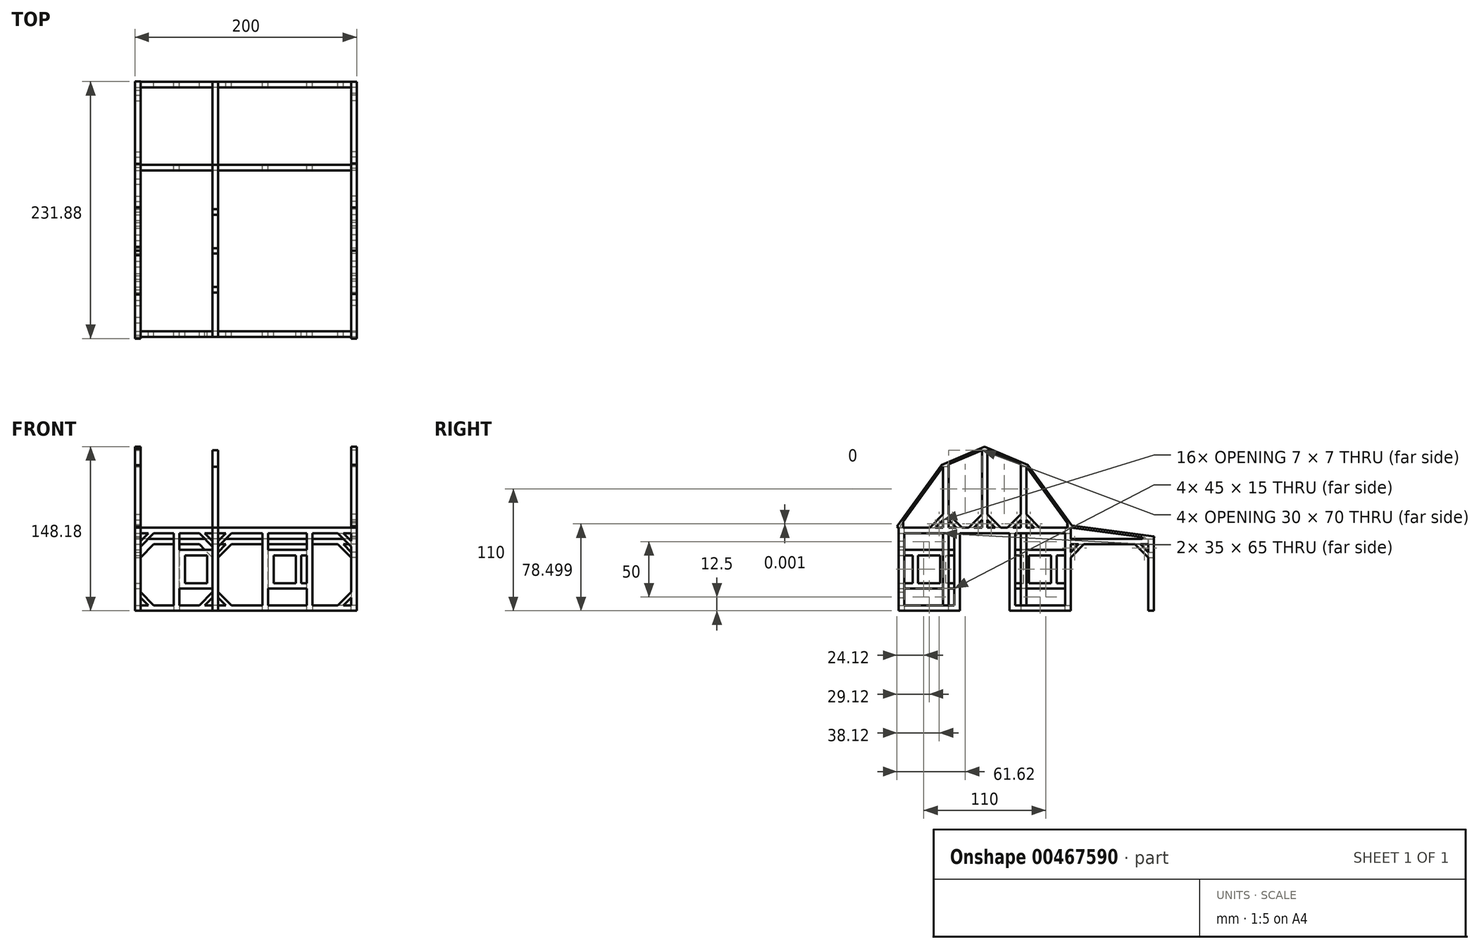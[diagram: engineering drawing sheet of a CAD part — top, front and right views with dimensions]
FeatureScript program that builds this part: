
annotation { "Feature Type Name" : "Feature", "Feature Type Description" : "" }
export const myFeature = defineFeature(function(context is Context, id is Id, definition is map)
    precondition{}
    {
        {
            var Q0;
            Q0=qCreatedBy(makeId("Front.planeOp"),FACE);
            var sketch = newSketch(context, id + "F0", { "sketchPlane" : qUnion([Q0])});
            skLineSegment(sketch, "E0", {"start": v(-73.98, 70) * mm, "end": v(-73.98, 65) * mm});
            skLineSegment(sketch, "E1", {"start": v(-73.98, 0) * mm, "end": v(-73.98, -5) * mm});
            skLineSegment(sketch, "E2", {"start": v(116.02, -5) * mm, "end": v(116.02, 0) * mm});
            skLineSegment(sketch, "E3", {"start": v(116.02, 70) * mm, "end": v(116.02, 65) * mm});
            skLineSegment(sketch, "E4", {"start": v(76.02, 65) * mm, "end": v(41.02, 65) * mm});
            skLineSegment(sketch, "E5", {"start": v(76.02, 0) * mm, "end": v(41.02, 0) * mm});
            skLineSegment(sketch, "E6", {"start": v(-8.98, 65) * mm, "end": v(-8.98, 70) * mm});
            skLineSegment(sketch, "E7", {"start": v(-3.98, 65) * mm, "end": v(-3.98, 70) * mm});
            skLineSegment(sketch, "E8", {"start": v(-8.98, 0) * mm, "end": v(-8.98, -5) * mm});
            skLineSegment(sketch, "E9", {"start": v(-3.98, 0) * mm, "end": v(-3.98, -5) * mm});
            skLineSegment(sketch, "E10", {"start": v(-73.98, 70) * mm, "end": v(-8.98, 70) * mm});
            skLineSegment(sketch, "E11", {"start": v(-73.98, -5) * mm, "end": v(-8.98, -5) * mm});
            skLineSegment(sketch, "E12", {"start": v(-3.98, 70) * mm, "end": v(116.02, 70) * mm});
            skLineSegment(sketch, "E13", {"start": v(-3.98, -5) * mm, "end": v(116.02, -5) * mm});
            skLineSegment(sketch, "E14", {"start": v(-73.98, 58) * mm, "end": v(-73.98, 53) * mm});
            skLineSegment(sketch, "E15", {"start": v(-73.98, 65) * mm, "end": v(-66.98, 65) * mm});
            skLineSegment(sketch, "E16", {"start": v(-73.98, 58) * mm, "end": v(-66.98, 65) * mm});
            skLineSegment(sketch, "E17", {"start": v(-73.98, 53) * mm, "end": v(-61.98, 65) * mm});
            skLineSegment(sketch, "E18", {"start": v(-73.98, 7) * mm, "end": v(-73.98, 12) * mm});
            skLineSegment(sketch, "E19", {"start": v(-73.98, 0) * mm, "end": v(-66.98, 0) * mm});
            skLineSegment(sketch, "E20", {"start": v(-66.98, 0) * mm, "end": v(-73.98, 7) * mm});
            skLineSegment(sketch, "E21", {"start": v(-61.98, 0) * mm, "end": v(-73.98, 12) * mm});
            skLineSegment(sketch, "E22", {"start": v(-8.98, 65) * mm, "end": v(-15.98, 65) * mm});
            skLineSegment(sketch, "E23", {"start": v(-8.98, 58) * mm, "end": v(-8.98, 53) * mm});
            skLineSegment(sketch, "E24", {"start": v(-15.98, 65) * mm, "end": v(-8.98, 58) * mm});
            skLineSegment(sketch, "E25", {"start": v(-20.98, 65) * mm, "end": v(-8.98, 53) * mm});
            skLineSegment(sketch, "E26", {"start": v(-8.98, 7) * mm, "end": v(-8.98, 12) * mm});
            skLineSegment(sketch, "E27", {"start": v(-8.98, 0) * mm, "end": v(-15.98, 0) * mm});
            skLineSegment(sketch, "E28", {"start": v(-15.98, 0) * mm, "end": v(-8.98, 7) * mm});
            skLineSegment(sketch, "E29", {"start": v(-20.98, 0) * mm, "end": v(-8.98, 12) * mm});
            skLineSegment(sketch, "E30", {"start": v(-3.98, 58) * mm, "end": v(-3.98, 53) * mm});
            skLineSegment(sketch, "E31", {"start": v(-3.98, 7) * mm, "end": v(-3.98, 12) * mm});
            skLineSegment(sketch, "E32", {"start": v(-3.98, 65) * mm, "end": v(3.02, 65) * mm});
            skLineSegment(sketch, "E33", {"start": v(-3.98, 58) * mm, "end": v(3.02, 65) * mm});
            skLineSegment(sketch, "E34", {"start": v(-3.98, 53) * mm, "end": v(8.02, 65) * mm});
            skLineSegment(sketch, "E35", {"start": v(-3.98, 0) * mm, "end": v(3.02, 0) * mm});
            skLineSegment(sketch, "E36", {"start": v(-3.98, 7) * mm, "end": v(3.02, 0) * mm});
            skLineSegment(sketch, "E37", {"start": v(-3.98, 12) * mm, "end": v(8.02, 0) * mm});
            skLineSegment(sketch, "E38", {"start": v(116.02, 65) * mm, "end": v(109.02, 65) * mm});
            skLineSegment(sketch, "E39", {"start": v(116.02, 58) * mm, "end": v(116.02, 53) * mm});
            skLineSegment(sketch, "E40", {"start": v(109.02, 65) * mm, "end": v(116.02, 58) * mm});
            skLineSegment(sketch, "E41", {"start": v(104.02, 65) * mm, "end": v(116.02, 53) * mm});
            skLineSegment(sketch, "E42", {"start": v(116.02, 7) * mm, "end": v(116.02, 12) * mm});
            skLineSegment(sketch, "E43", {"start": v(116.02, 0) * mm, "end": v(109.02, 0) * mm});
            skLineSegment(sketch, "E44", {"start": v(109.02, 0) * mm, "end": v(116.02, 7) * mm});
            skLineSegment(sketch, "E45", {"start": v(104.02, 0) * mm, "end": v(116.02, 12) * mm});
            skLineSegment(sketch, "E46", {"start": v(-61.98, 65) * mm, "end": v(-43.98, 65) * mm});
            skLineSegment(sketch, "E47", {"start": v(-61.98, 0) * mm, "end": v(-43.98, 0) * mm});
            skLineSegment(sketch, "E48", {"start": v(-20.98, 65) * mm, "end": v(-38.98, 65) * mm});
            skLineSegment(sketch, "E49", {"start": v(8.02, 65) * mm, "end": v(36.02, 65) * mm});
            skLineSegment(sketch, "E50", {"start": v(-20.98, 0) * mm, "end": v(-38.98, 0) * mm});
            skLineSegment(sketch, "E51", {"start": v(104.02, 65) * mm, "end": v(81.02, 65) * mm});
            skLineSegment(sketch, "E52", {"start": v(104.02, 0) * mm, "end": v(81.02, 0) * mm});
            skLineSegment(sketch, "E53", {"start": v(8.02, 0) * mm, "end": v(36.02, 0) * mm});
            skLineSegment(sketch, "E54", {"start": v(-43.98, 65) * mm, "end": v(-43.98, 0) * mm});
            skLineSegment(sketch, "E55", {"start": v(36.02, 65) * mm, "end": v(36.02, 0) * mm});
            skLineSegment(sketch, "E56", {"start": v(81.02, 65) * mm, "end": v(81.02, 0) * mm});
            skLineSegment(sketch, "E57", {"start": v(41.02, 0) * mm, "end": v(41.02, 15) * mm});
            skLineSegment(sketch, "E58", {"start": v(41.02, 50) * mm, "end": v(41.02, 65) * mm});
            skLineSegment(sketch, "E59", {"start": v(76.02, 0) * mm, "end": v(76.02, 15) * mm});
            skLineSegment(sketch, "E60", {"start": v(76.02, 20) * mm, "end": v(76.02, 45) * mm});
            skLineSegment(sketch, "E61", {"start": v(76.02, 50) * mm, "end": v(76.02, 65) * mm});
            skLineSegment(sketch, "E62", {"start": v(41.02, 50) * mm, "end": v(76.02, 50) * mm});
            skLineSegment(sketch, "E63", {"start": v(41.02, 15) * mm, "end": v(76.02, 15) * mm});
            skLineSegment(sketch, "E64", {"start": v(76.02, 20) * mm, "end": v(71.02, 20) * mm});
            skLineSegment(sketch, "E65", {"start": v(76.02, 45) * mm, "end": v(71.02, 45) * mm});
            skLineSegment(sketch, "E66", {"start": v(71.02, 45) * mm, "end": v(71.02, 20) * mm});
            skLineSegment(sketch, "E67", {"start": v(46.02, 45) * mm, "end": v(46.02, 20) * mm});
            skLineSegment(sketch, "E68", {"start": v(46.02, 45) * mm, "end": v(66.02, 45) * mm});
            skLineSegment(sketch, "E69", {"start": v(46.02, 20) * mm, "end": v(66.02, 20) * mm});
            skLineSegment(sketch, "E70", {"start": v(66.02, 45) * mm, "end": v(66.02, 20) * mm});
            skLineSegment(sketch, "E71", {"start": v(-38.98, 0) * mm, "end": v(-38.98, 15) * mm});
            skLineSegment(sketch, "E72", {"start": v(-38.98, 50) * mm, "end": v(-38.98, 65) * mm});
            skLineSegment(sketch, "E73", {"start": v(-38.98, 15) * mm, "end": v(-8.98, 15) * mm});
            skLineSegment(sketch, "E74", {"start": v(-38.98, 50) * mm, "end": v(-8.98, 50) * mm});
            skLineSegment(sketch, "E75", {"start": v(-33.98, 45) * mm, "end": v(-33.98, 20) * mm});
            skLineSegment(sketch, "E76", {"start": v(-13.98, 45) * mm, "end": v(-13.98, 20) * mm});
            skLineSegment(sketch, "E77", {"start": v(-33.98, 20) * mm, "end": v(-13.98, 20) * mm});
            skLineSegment(sketch, "E78", {"start": v(-33.98, 45) * mm, "end": v(-13.98, 45) * mm});
            skLineSegment(sketch, "E79", {"start": v(-8.98, 15) * mm, "end": v(-8.98, 50) * mm});
            skSolve(sketch);
        }
        {
            var Q0;
            Q0 = qSketchRegion(id + "F0", true);
            extrude(context, id + "F1", {"entities" : qUnion([Q0]), "depth" : 5 * mm});
        }
        {
            var Q0;
            Q0=makeQuery(id+"F1.opExtrude","SWEPT_FACE",FACE,{"disambiguationData":[OSD([sQuery(id+"F0.wireOp",EDGE,"E1")])]});
            var sketch = newSketch(context, id + "F2", { "sketchPlane" : qUnion([Q0])});
            skLineSegment(sketch, "E80", {"start": v(5, -5) * mm, "end": v(5, 70) * mm});
            skLineSegment(sketch, "E81", {"start": v(-150, 70) * mm, "end": v(-150, 60) * mm});
            skLineSegment(sketch, "E82", {"start": v(-225, 60) * mm, "end": v(-225, -5) * mm});
            skLineSegment(sketch, "E83", {"start": v(-225, -5) * mm, "end": v(-220, -5) * mm});
            skLineSegment(sketch, "E84", {"start": v(-150, 55) * mm, "end": v(-150, 48) * mm});
            skLineSegment(sketch, "E85", {"start": v(-150, 55) * mm, "end": v(-157, 55) * mm});
            skLineSegment(sketch, "E86", {"start": v(-157, 55) * mm, "end": v(-150, 48) * mm});
            skLineSegment(sketch, "E87", {"start": v(-162, 55) * mm, "end": v(-150, 43) * mm});
            skLineSegment(sketch, "E88", {"start": v(-220, 55) * mm, "end": v(-220, 48) * mm});
            skLineSegment(sketch, "E89", {"start": v(-220, 55) * mm, "end": v(-213, 55) * mm});
            skLineSegment(sketch, "E90", {"start": v(-220, 48) * mm, "end": v(-213, 55) * mm});
            skLineSegment(sketch, "E91", {"start": v(-220, 43) * mm, "end": v(-208, 55) * mm});
            skLineSegment(sketch, "E92", {"start": v(-110, 70) * mm, "end": v(-110, 77) * mm});
            skLineSegment(sketch, "E93", {"start": v(-110, 70) * mm, "end": v(-117, 70) * mm});
            skLineSegment(sketch, "E94", {"start": v(-117, 70) * mm, "end": v(-110, 77) * mm});
            skLineSegment(sketch, "E95", {"start": v(-122, 70) * mm, "end": v(-110, 82) * mm});
            skLineSegment(sketch, "E96", {"start": v(-105, 70) * mm, "end": v(-105, 77) * mm});
            skLineSegment(sketch, "E97", {"start": v(-105, 70) * mm, "end": v(-98, 70) * mm});
            skLineSegment(sketch, "E98", {"start": v(-98, 70) * mm, "end": v(-105, 77) * mm});
            skLineSegment(sketch, "E99", {"start": v(-93, 70) * mm, "end": v(-105, 82) * mm});
            skLineSegment(sketch, "E100", {"start": v(-75, 70) * mm, "end": v(-75, 77) * mm});
            skLineSegment(sketch, "E101", {"start": v(-75, 70) * mm, "end": v(-82, 70) * mm});
            skLineSegment(sketch, "E102", {"start": v(-82, 70) * mm, "end": v(-75, 77) * mm});
            skLineSegment(sketch, "E103", {"start": v(-87, 70) * mm, "end": v(-75, 82) * mm});
            skLineSegment(sketch, "E104", {"start": v(-70, 70) * mm, "end": v(-70, 77) * mm});
            skLineSegment(sketch, "E105", {"start": v(-70, 70) * mm, "end": v(-63, 70) * mm});
            skLineSegment(sketch, "E106", {"start": v(-70, 77) * mm, "end": v(-63, 70) * mm});
            skLineSegment(sketch, "E107", {"start": v(-58, 70) * mm, "end": v(-70, 82) * mm});
            skLineSegment(sketch, "E108", {"start": v(-40, 70) * mm, "end": v(-40, 77) * mm});
            skLineSegment(sketch, "E109", {"start": v(-40, 70) * mm, "end": v(-47, 70) * mm});
            skLineSegment(sketch, "E110", {"start": v(-47, 70) * mm, "end": v(-40, 77) * mm});
            skLineSegment(sketch, "E111", {"start": v(-52, 70) * mm, "end": v(-40, 82) * mm});
            skLineSegment(sketch, "E112", {"start": v(-35, 70) * mm, "end": v(-35, 77) * mm});
            skLineSegment(sketch, "E113", {"start": v(-35, 70) * mm, "end": v(-28, 70) * mm});
            skLineSegment(sketch, "E114", {"start": v(-28, 70) * mm, "end": v(-35, 77) * mm});
            skLineSegment(sketch, "E115", {"start": v(-23, 70) * mm, "end": v(-35, 82) * mm});
            skLineSegment(sketch, "E116", {"start": v(5, 70) * mm, "end": v(6.62, 71.18) * mm});
            skLineSegment(sketch, "E117", {"start": v(6.62, 71.18) * mm, "end": v(-33.35, 126.13) * mm});
            skLineSegment(sketch, "E118", {"start": v(-33.35, 126.13) * mm, "end": v(-68.47, 141.18) * mm});
            skLineSegment(sketch, "E119", {"start": v(-68.47, 141.18) * mm, "end": v(-72.5, 143.18) * mm});
            skLineSegment(sketch, "E120", {"start": v(-225, 60) * mm, "end": v(-225.26, 61.98) * mm});
            skLineSegment(sketch, "E121", {"start": v(-225.26, 61.98) * mm, "end": v(-151.2, 71.85) * mm});
            skLineSegment(sketch, "E122", {"start": v(-151.2, 71.85) * mm, "end": v(-111.54, 126.4) * mm});
            skLineSegment(sketch, "E123", {"start": v(-111.54, 126.4) * mm, "end": v(-76.19, 141.55) * mm});
            skLineSegment(sketch, "E124", {"start": v(-76.19, 141.55) * mm, "end": v(-72.5, 143.18) * mm});
            skLineSegment(sketch, "E125", {"start": v(-70, 140) * mm, "end": v(-40, 127.14) * mm});
            skLineSegment(sketch, "E126", {"start": v(-75, 140) * mm, "end": v(-105, 127.14) * mm});
            skLineSegment(sketch, "E127", {"start": v(-147.9, 72.9) * mm, "end": v(-147.9, 70) * mm});
            skLineSegment(sketch, "E128", {"start": v(-110, 125) * mm, "end": v(-147.9, 72.9) * mm});
            skLineSegment(sketch, "E129", {"start": v(-147.9, 70) * mm, "end": v(-122, 70) * mm});
            skLineSegment(sketch, "E130", {"start": v(-110, 125) * mm, "end": v(-110, 82) * mm});
            skLineSegment(sketch, "E131", {"start": v(3.62, 71.9) * mm, "end": v(3.62, 70) * mm});
            skLineSegment(sketch, "E132", {"start": v(-35, 125) * mm, "end": v(3.62, 71.9) * mm});
            skLineSegment(sketch, "E133", {"start": v(-23, 70) * mm, "end": v(3.62, 70) * mm});
            skLineSegment(sketch, "E134", {"start": v(-35, 125) * mm, "end": v(-35, 82) * mm});
            skLineSegment(sketch, "E135", {"start": v(-217.53, 61) * mm, "end": v(-217.53, 60) * mm});
            skLineSegment(sketch, "E136", {"start": v(-217.53, 60) * mm, "end": v(-150, 60) * mm});
            skLineSegment(sketch, "E137", {"start": v(-217.53, 61) * mm, "end": v(-150, 70) * mm});
            skLineSegment(sketch, "E138", {"start": v(-220, 43) * mm, "end": v(-220, -5) * mm});
            skLineSegment(sketch, "E139", {"start": v(-208, 55) * mm, "end": v(-162, 55) * mm});
            skLineSegment(sketch, "E140", {"start": v(-150, 43) * mm, "end": v(-150, -5) * mm});
            skLineSegment(sketch, "E141", {"start": v(-93, 70) * mm, "end": v(-87, 70) * mm});
            skLineSegment(sketch, "E142", {"start": v(-58, 70) * mm, "end": v(-52, 70) * mm});
            skLineSegment(sketch, "E143", {"start": v(-75, 82) * mm, "end": v(-75, 140) * mm});
            skLineSegment(sketch, "E144", {"start": v(-70, 140) * mm, "end": v(-70, 82) * mm});
            skLineSegment(sketch, "E145", {"start": v(-40, 127.14) * mm, "end": v(-40, 82) * mm});
            skLineSegment(sketch, "E146", {"start": v(-105, 127.14) * mm, "end": v(-105, 82) * mm});
            skLineSegment(sketch, "E147", {"start": v(5, -5) * mm, "end": v(-50, -5) * mm});
            skPoint(sketch, "E147.endSnap0", {"position": v(2.5, -5) * mm});
            skLineSegment(sketch, "E148", {"start": v(-50, -5) * mm, "end": v(-50, 65) * mm});
            skLineSegment(sketch, "E149", {"start": v(-150, -5) * mm, "end": v(-95, -5) * mm});
            skLineSegment(sketch, "E150", {"start": v(-95, -5) * mm, "end": v(-95, 65) * mm});
            skLineSegment(sketch, "E151", {"start": v(-95, 65) * mm, "end": v(-50, 65) * mm});
            skLineSegment(sketch, "E152", {"start": v(-145, 65) * mm, "end": v(-100, 65) * mm});
            skLineSegment(sketch, "E153", {"start": v(-145, 0) * mm, "end": v(-100, 0) * mm});
            skLineSegment(sketch, "E154", {"start": v(-45, 65) * mm, "end": v(0, 65) * mm});
            skLineSegment(sketch, "E155", {"start": v(-45, 0) * mm, "end": v(0, 0) * mm});
            skLineSegment(sketch, "E156", {"start": v(-145, 15) * mm, "end": v(-100, 15) * mm});
            skLineSegment(sketch, "E157", {"start": v(-145, 20) * mm, "end": v(-137.5, 20) * mm});
            skLineSegment(sketch, "E158", {"start": v(-100, 20) * mm, "end": v(-107.5, 20) * mm});
            skLineSegment(sketch, "E159", {"start": v(-107.5, 20) * mm, "end": v(-107.5, 45) * mm});
            skLineSegment(sketch, "E160", {"start": v(-137.5, 20) * mm, "end": v(-137.5, 45) * mm});
            skLineSegment(sketch, "E161", {"start": v(-137.5, 45) * mm, "end": v(-145, 45) * mm});
            skLineSegment(sketch, "E162", {"start": v(-107.5, 45) * mm, "end": v(-100, 45) * mm});
            skLineSegment(sketch, "E163", {"start": v(-145, 50) * mm, "end": v(-100, 50) * mm});
            skLineSegment(sketch, "E164", {"start": v(-132.5, 20) * mm, "end": v(-112.5, 20) * mm});
            skLineSegment(sketch, "E165", {"start": v(-132.5, 45) * mm, "end": v(-132.5, 20) * mm});
            skLineSegment(sketch, "E166", {"start": v(-132.5, 45) * mm, "end": v(-112.5, 45) * mm});
            skLineSegment(sketch, "E167", {"start": v(-112.5, 45) * mm, "end": v(-112.5, 20) * mm});
            skLineSegment(sketch, "E168", {"start": v(-45, 15) * mm, "end": v(0, 15) * mm});
            skLineSegment(sketch, "E169", {"start": v(-45, 20) * mm, "end": v(-37.5, 20) * mm});
            skLineSegment(sketch, "E170", {"start": v(0, 20) * mm, "end": v(-7.5, 20) * mm});
            skLineSegment(sketch, "E171", {"start": v(-37.5, 20) * mm, "end": v(-37.5, 45) * mm});
            skLineSegment(sketch, "E172", {"start": v(-7.5, 20) * mm, "end": v(-7.5, 45) * mm});
            skLineSegment(sketch, "E173", {"start": v(-7.5, 45) * mm, "end": v(0, 45) * mm});
            skLineSegment(sketch, "E174", {"start": v(-37.5, 45) * mm, "end": v(-45, 45) * mm});
            skLineSegment(sketch, "E175", {"start": v(-45, 50) * mm, "end": v(0, 50) * mm});
            skLineSegment(sketch, "E176", {"start": v(-32.5, 45) * mm, "end": v(-32.5, 20) * mm});
            skLineSegment(sketch, "E177", {"start": v(-32.5, 45) * mm, "end": v(-12.5, 45) * mm});
            skLineSegment(sketch, "E178", {"start": v(-12.5, 45) * mm, "end": v(-12.5, 20) * mm});
            skLineSegment(sketch, "E179", {"start": v(-32.5, 20) * mm, "end": v(-12.5, 20) * mm});
            skLineSegment(sketch, "E180", {"start": v(-145, 65) * mm, "end": v(-145, 50) * mm});
            skLineSegment(sketch, "E181", {"start": v(-145, 45) * mm, "end": v(-145, 20) * mm});
            skLineSegment(sketch, "E182", {"start": v(-145, 15) * mm, "end": v(-145, 0) * mm});
            skLineSegment(sketch, "E183", {"start": v(-100, 65) * mm, "end": v(-100, 50) * mm});
            skLineSegment(sketch, "E184", {"start": v(-100, 45) * mm, "end": v(-100, 20) * mm});
            skLineSegment(sketch, "E185", {"start": v(-100, 15) * mm, "end": v(-100, 0) * mm});
            skLineSegment(sketch, "E186", {"start": v(-45, 65) * mm, "end": v(-45, 50) * mm});
            skLineSegment(sketch, "E187", {"start": v(-45, 45) * mm, "end": v(-45, 20) * mm});
            skLineSegment(sketch, "E188", {"start": v(-45, 15) * mm, "end": v(-45, 0) * mm});
            skLineSegment(sketch, "E189", {"start": v(0, 65) * mm, "end": v(0, 50) * mm});
            skLineSegment(sketch, "E190", {"start": v(0, 45) * mm, "end": v(0, 20) * mm});
            skLineSegment(sketch, "E191", {"start": v(0, 15) * mm, "end": v(0, 0) * mm});
            skSolve(sketch);
        }
        {
            var Q0;
            Q0 = qSketchRegion(id + "F2", true);
            extrude(context, id + "F3", {"entities" : qUnion([Q0]), "depth" : 5 * mm});
        }
        {
            var Q0;
            Q0=makeQuery(id+"F1.opExtrude","SWEPT_FACE",FACE,{"disambiguationData":[OSD([sQuery(id+"F0.wireOp",EDGE,"E3")])]});
            var sketch = newSketch(context, id + "F4", { "sketchPlane" : qUnion([Q0])});
            skLineSegment(sketch, "E192", {"start": v(-5, -5) * mm, "end": v(50, -5) * mm});
            skLineSegment(sketch, "E193", {"start": v(50, -5) * mm, "end": v(50, 65) * mm});
            skLineSegment(sketch, "E194", {"start": v(50, 65) * mm, "end": v(95, 65) * mm});
            skLineSegment(sketch, "E195", {"start": v(95, 65) * mm, "end": v(95, -5) * mm});
            skLineSegment(sketch, "E196", {"start": v(95, -5) * mm, "end": v(150, -5) * mm});
            skLineSegment(sketch, "E197", {"start": v(150, 60) * mm, "end": v(150, 70) * mm});
            skLineSegment(sketch, "E198", {"start": v(45, 65) * mm, "end": v(45, 0) * mm});
            skLineSegment(sketch, "E199", {"start": v(45, 0) * mm, "end": v(0, 0) * mm});
            skLineSegment(sketch, "E200", {"start": v(0, 0) * mm, "end": v(0, 65) * mm});
            skLineSegment(sketch, "E201", {"start": v(0, 65) * mm, "end": v(45, 65) * mm});
            skLineSegment(sketch, "E202", {"start": v(100, 65) * mm, "end": v(100, 0) * mm});
            skLineSegment(sketch, "E203", {"start": v(100, 0) * mm, "end": v(145, 0) * mm});
            skLineSegment(sketch, "E204", {"start": v(145, 0) * mm, "end": v(145, 65) * mm});
            skLineSegment(sketch, "E205", {"start": v(145, 65) * mm, "end": v(100, 65) * mm});
            skLineSegment(sketch, "E206", {"start": v(225, -5) * mm, "end": v(220, -5) * mm});
            skLineSegment(sketch, "E207", {"start": v(150, 55) * mm, "end": v(150, 48) * mm});
            skLineSegment(sketch, "E208", {"start": v(150, 55) * mm, "end": v(157, 55) * mm});
            skLineSegment(sketch, "E209", {"start": v(150, 48) * mm, "end": v(157, 55) * mm});
            skLineSegment(sketch, "E210", {"start": v(150, 43) * mm, "end": v(162, 55) * mm});
            skLineSegment(sketch, "E211", {"start": v(220, 55) * mm, "end": v(220, 48) * mm});
            skLineSegment(sketch, "E212", {"start": v(220, 55) * mm, "end": v(213, 55) * mm});
            skLineSegment(sketch, "E213", {"start": v(213, 55) * mm, "end": v(220, 48) * mm});
            skLineSegment(sketch, "E214", {"start": v(208, 55) * mm, "end": v(220, 43) * mm});
            skLineSegment(sketch, "E215", {"start": v(110, 70) * mm, "end": v(110, 77) * mm});
            skLineSegment(sketch, "E216", {"start": v(110, 70) * mm, "end": v(117, 70) * mm});
            skLineSegment(sketch, "E217", {"start": v(122, 70) * mm, "end": v(110, 82) * mm});
            skLineSegment(sketch, "E218", {"start": v(110, 77) * mm, "end": v(117, 70) * mm});
            skLineSegment(sketch, "E219", {"start": v(105, 70) * mm, "end": v(105, 77) * mm});
            skLineSegment(sketch, "E220", {"start": v(105, 70) * mm, "end": v(98, 70) * mm});
            skLineSegment(sketch, "E221", {"start": v(98, 70) * mm, "end": v(105, 77) * mm});
            skLineSegment(sketch, "E222", {"start": v(93, 70) * mm, "end": v(105, 82) * mm});
            skLineSegment(sketch, "E223", {"start": v(75, 70) * mm, "end": v(75, 77) * mm});
            skLineSegment(sketch, "E224", {"start": v(75, 70) * mm, "end": v(82, 70) * mm});
            skLineSegment(sketch, "E225", {"start": v(75, 77) * mm, "end": v(82, 70) * mm});
            skLineSegment(sketch, "E226", {"start": v(75, 82) * mm, "end": v(87, 70) * mm});
            skLineSegment(sketch, "E227", {"start": v(70, 70) * mm, "end": v(70, 77) * mm});
            skLineSegment(sketch, "E228", {"start": v(70, 70) * mm, "end": v(63, 70) * mm});
            skLineSegment(sketch, "E229", {"start": v(63, 70) * mm, "end": v(70, 77) * mm});
            skLineSegment(sketch, "E230", {"start": v(58, 70) * mm, "end": v(70, 82) * mm});
            skLineSegment(sketch, "E231", {"start": v(40, 70) * mm, "end": v(40, 77) * mm});
            skLineSegment(sketch, "E232", {"start": v(40, 70) * mm, "end": v(47, 70) * mm});
            skLineSegment(sketch, "E233", {"start": v(40, 77) * mm, "end": v(47, 70) * mm});
            skLineSegment(sketch, "E234", {"start": v(40, 82) * mm, "end": v(52, 70) * mm});
            skLineSegment(sketch, "E235", {"start": v(35, 70) * mm, "end": v(35, 77) * mm});
            skLineSegment(sketch, "E236", {"start": v(35, 70) * mm, "end": v(28, 70) * mm});
            skLineSegment(sketch, "E237", {"start": v(28, 70) * mm, "end": v(35, 77) * mm});
            skLineSegment(sketch, "E238", {"start": v(23, 70) * mm, "end": v(35, 82) * mm});
            skLineSegment(sketch, "E239", {"start": v(35, 125) * mm, "end": v(35, 82) * mm});
            skLineSegment(sketch, "E240", {"start": v(52, 70) * mm, "end": v(58, 70) * mm});
            skLineSegment(sketch, "E241", {"start": v(70, 82) * mm, "end": v(70, 140) * mm});
            skLineSegment(sketch, "E242", {"start": v(87, 70) * mm, "end": v(93, 70) * mm});
            skLineSegment(sketch, "E243", {"start": v(75, 82) * mm, "end": v(75, 140) * mm});
            skLineSegment(sketch, "E244", {"start": v(110, 82) * mm, "end": v(110, 125) * mm});
            skLineSegment(sketch, "E245", {"start": v(162, 55) * mm, "end": v(208, 55) * mm});
            skLineSegment(sketch, "E246", {"start": v(150, 43) * mm, "end": v(150, -5) * mm});
            skLineSegment(sketch, "E247", {"start": v(220, 43) * mm, "end": v(220, -5) * mm});
            skLineSegment(sketch, "E248", {"start": v(-5, 70) * mm, "end": v(-6.62, 71.18) * mm});
            skLineSegment(sketch, "E249", {"start": v(-6.62, 71.18) * mm, "end": v(33.58, 126.45) * mm});
            skLineSegment(sketch, "E250", {"start": v(72.5, 143.18) * mm, "end": v(111.54, 126.45) * mm});
            skLineSegment(sketch, "E251", {"start": v(111.54, 126.45) * mm, "end": v(151.25, 71.85) * mm});
            skLineSegment(sketch, "E252", {"start": v(151.25, 71.85) * mm, "end": v(225.1, 62) * mm});
            skLineSegment(sketch, "E253", {"start": v(214.65, 60) * mm, "end": v(214.65, 61.38) * mm});
            skLineSegment(sketch, "E254", {"start": v(214.65, 61.38) * mm, "end": v(150, 70) * mm});
            skLineSegment(sketch, "E255", {"start": v(150, 60) * mm, "end": v(214.65, 60) * mm});
            skLineSegment(sketch, "E256", {"start": v(146.96, 70) * mm, "end": v(146.96, 74.18) * mm});
            skLineSegment(sketch, "E257", {"start": v(122, 70) * mm, "end": v(146.96, 70) * mm});
            skLineSegment(sketch, "E258", {"start": v(110, 125) * mm, "end": v(146.96, 74.18) * mm});
            skLineSegment(sketch, "E259", {"start": v(-1, 70) * mm, "end": v(-1, 75.5) * mm});
            skLineSegment(sketch, "E260", {"start": v(35, 125) * mm, "end": v(-1, 75.5) * mm});
            skLineSegment(sketch, "E261", {"start": v(40, 127.14) * mm, "end": v(70, 140) * mm});
            skLineSegment(sketch, "E262", {"start": v(40, 127.14) * mm, "end": v(40, 82) * mm});
            skLineSegment(sketch, "E263", {"start": v(75, 140) * mm, "end": v(105, 127.14) * mm});
            skLineSegment(sketch, "E264", {"start": v(105, 127.14) * mm, "end": v(105, 82) * mm});
            skLineSegment(sketch, "E265", {"start": v(33.58, 126.45) * mm, "end": v(72.5, 143.18) * mm});
            skLineSegment(sketch, "E266", {"start": v(225, -5) * mm, "end": v(225.1, 62) * mm});
            skLineSegment(sketch, "E267", {"start": v(-5, -5) * mm, "end": v(-5, 70) * mm});
            skLineSegment(sketch, "E268", {"start": v(23, 70) * mm, "end": v(-1, 70) * mm});
            skSolve(sketch);
        }
        {
            var Q0;
            Q0 = qSketchRegion(id + "F4", true);
            extrude(context, id + "F5", {"entities" : qUnion([Q0]), "operationType" : NewBodyOperationType.ADD, "depth" : 5 * mm});
        }
        {
            var Q0;
            Q0=makeQuery(id+"F5.opExtrude","SWEPT_FACE",FACE,{"disambiguationData":[OSD([sQuery(id+"F4.wireOp",EDGE,"58TneIG1-xEIF-bJ1H-MJ4t-spUmvF1AfA7A"),sQuery(id+"F4.wireOp",EDGE,"vosEks8g-I7cK-nT4N-e65d-MzGEJBJkZxlQ"),sQuery(id+"F4.wireOp",EDGE,"E197")])]});
            var sketch = newSketch(context, id + "F6", { "sketchPlane" : qUnion([Q0])});
            skLineSegment(sketch, "E269", {"start": v(-36.02, 0) * mm, "end": v(3.98, 0) * mm});
            skLineSegment(sketch, "E270", {"start": v(3.98, 0) * mm, "end": v(3.98, -5) * mm});
            skLineSegment(sketch, "E271", {"start": v(3.98, -5) * mm, "end": v(-116.02, -5) * mm});
            skLineSegment(sketch, "E272", {"start": v(-116.02, -5) * mm, "end": v(-116.02, 0) * mm});
            skLineSegment(sketch, "E273", {"start": v(-116.02, 0) * mm, "end": v(-81.02, 0) * mm});
            skLineSegment(sketch, "E274", {"start": v(-81.02, 0) * mm, "end": v(-81.02, 65) * mm});
            skLineSegment(sketch, "E275", {"start": v(-76.02, 65) * mm, "end": v(-76.02, 0) * mm});
            skLineSegment(sketch, "E276", {"start": v(-76.02, 0) * mm, "end": v(-41.02, 0) * mm});
            skLineSegment(sketch, "E277", {"start": v(-41.02, 0) * mm, "end": v(-41.02, 65) * mm});
            skLineSegment(sketch, "E278", {"start": v(-41.02, 65) * mm, "end": v(-76.02, 65) * mm});
            skLineSegment(sketch, "E279", {"start": v(8.98, 70) * mm, "end": v(8.98, 65) * mm});
            skLineSegment(sketch, "E280", {"start": v(8.98, 70) * mm, "end": v(73.98, 70) * mm});
            skLineSegment(sketch, "E281", {"start": v(73.98, 70) * mm, "end": v(73.98, 65) * mm});
            skLineSegment(sketch, "E282", {"start": v(73.98, 65) * mm, "end": v(43.98, 65) * mm});
            skLineSegment(sketch, "E283", {"start": v(43.98, 65) * mm, "end": v(43.98, 0) * mm});
            skLineSegment(sketch, "E284", {"start": v(43.98, 0) * mm, "end": v(73.98, 0) * mm});
            skLineSegment(sketch, "E285", {"start": v(73.98, 0) * mm, "end": v(73.98, -5) * mm});
            skLineSegment(sketch, "E286", {"start": v(73.98, -5) * mm, "end": v(8.98, -5) * mm});
            skLineSegment(sketch, "E287", {"start": v(8.98, -5) * mm, "end": v(8.98, 0) * mm});
            skLineSegment(sketch, "E288", {"start": v(8.98, 0) * mm, "end": v(38.98, 0) * mm});
            skLineSegment(sketch, "E289", {"start": v(38.98, 0) * mm, "end": v(38.98, 65) * mm});
            skLineSegment(sketch, "E290", {"start": v(38.98, 65) * mm, "end": v(8.98, 65) * mm});
            skLineSegment(sketch, "E291", {"start": v(-36.02, 0) * mm, "end": v(-36.02, 65) * mm});
            skLineSegment(sketch, "E292", {"start": v(-36.02, 65) * mm, "end": v(3.98, 65) * mm});
            skLineSegment(sketch, "E293", {"start": v(-81.02, 65) * mm, "end": v(-116.02, 65) * mm});
            skLineSegment(sketch, "E294", {"start": v(-116.02, 65) * mm, "end": v(-116.02, 70) * mm});
            skLineSegment(sketch, "E295", {"start": v(3.98, 65) * mm, "end": v(3.98, 70) * mm});
            skLineSegment(sketch, "E296", {"start": v(-116.02, 70) * mm, "end": v(3.98, 70) * mm});
            skSolve(sketch);
        }
        {
            var Q0;
            Q0 = qSketchRegion(id + "F6", true);
            extrude(context, id + "F7", {"entities" : qUnion([Q0]), "oppositeDirection" : true, "depth" : 5 * mm});
        }
        {
            var Q0;
            Q0=makeQuery(id+"F1.opExtrude","SWEPT_FACE",FACE,{"disambiguationData":[OSD([sQuery(id+"F0.wireOp",EDGE,"E6")])]});
            var sketch = newSketch(context, id + "F8", { "sketchPlane" : qUnion([Q0])});
            skLineSegment(sketch, "E297", {"start": v(-5, 70) * mm, "end": v(-5, -5) * mm});
            skLineSegment(sketch, "E298", {"start": v(-5, -5) * mm, "end": v(40, -5) * mm});
            skLineSegment(sketch, "E299", {"start": v(40, -5) * mm, "end": v(40, 65) * mm});
            skLineSegment(sketch, "E300", {"start": v(40, 65) * mm, "end": v(105, 65) * mm});
            skLineSegment(sketch, "E301", {"start": v(105, 65) * mm, "end": v(105, -5) * mm});
            skLineSegment(sketch, "E302", {"start": v(105, -5) * mm, "end": v(150, -5) * mm});
            skLineSegment(sketch, "E303", {"start": v(150, -5) * mm, "end": v(150, 55) * mm});
            skLineSegment(sketch, "E304", {"start": v(150, 55) * mm, "end": v(150, 60) * mm});
            skLineSegment(sketch, "E305", {"start": v(150, 60) * mm, "end": v(150, 70) * mm});
            skLineSegment(sketch, "E306", {"start": v(150, 60) * mm, "end": v(225, 60) * mm});
            skLineSegment(sketch, "E307", {"start": v(150, 55) * mm, "end": v(220, 55) * mm});
            skLineSegment(sketch, "E308", {"start": v(225, 60) * mm, "end": v(225, -5) * mm});
            skLineSegment(sketch, "E309", {"start": v(220, 55) * mm, "end": v(220, -5) * mm});
            skLineSegment(sketch, "E310", {"start": v(220, -5) * mm, "end": v(225, -5) * mm});
            skLineSegment(sketch, "E311", {"start": v(150, 70) * mm, "end": v(110, 70) * mm});
            skLineSegment(sketch, "E312", {"start": v(110, 70) * mm, "end": v(110, 125) * mm});
            skLineSegment(sketch, "E313", {"start": v(110, 125) * mm, "end": v(105, 125) * mm});
            skLineSegment(sketch, "E314", {"start": v(105, 125) * mm, "end": v(105, 70) * mm});
            skLineSegment(sketch, "E315", {"start": v(105, 70) * mm, "end": v(75, 70) * mm});
            skLineSegment(sketch, "E316", {"start": v(75, 70) * mm, "end": v(75, 140) * mm});
            skLineSegment(sketch, "E317", {"start": v(75, 140) * mm, "end": v(70, 140) * mm});
            skLineSegment(sketch, "E318", {"start": v(70, 140) * mm, "end": v(70, 70) * mm});
            skLineSegment(sketch, "E319", {"start": v(70, 70) * mm, "end": v(40, 70) * mm});
            skLineSegment(sketch, "E320", {"start": v(40, 70) * mm, "end": v(40, 125) * mm});
            skLineSegment(sketch, "E321", {"start": v(40, 125) * mm, "end": v(35, 125) * mm});
            skLineSegment(sketch, "E322", {"start": v(35, 125) * mm, "end": v(35, 70) * mm});
            skLineSegment(sketch, "E323", {"start": v(35, 70) * mm, "end": v(-5, 70) * mm});
            skLineSegment(sketch, "E324", {"start": v(35, 65) * mm, "end": v(35, 0) * mm});
            skLineSegment(sketch, "E325", {"start": v(35, 0) * mm, "end": v(0, 0) * mm});
            skLineSegment(sketch, "E326", {"start": v(0, 0) * mm, "end": v(0, 65) * mm});
            skLineSegment(sketch, "E327", {"start": v(0, 65) * mm, "end": v(35, 65) * mm});
            skLineSegment(sketch, "E328", {"start": v(110, 65) * mm, "end": v(110, 0) * mm});
            skLineSegment(sketch, "E329", {"start": v(110, 0) * mm, "end": v(145, 0) * mm});
            skLineSegment(sketch, "E330", {"start": v(145, 0) * mm, "end": v(145, 65) * mm});
            skLineSegment(sketch, "E331", {"start": v(145, 65) * mm, "end": v(110, 65) * mm});
            skSolve(sketch);
        }
        {
            var Q0;
            Q0 = qSketchRegion(id + "F8", true);
            extrude(context, id + "F9", {"entities" : qUnion([Q0]), "depth" : 5 * mm});
        }
        {
            var Q0;
            Q0=makeQuery(id+"F3.opExtrude","SWEPT_FACE",FACE,{"disambiguationData":[OSD([sQuery(id+"F2.wireOp",EDGE,"E82")])]});
            var sketch = newSketch(context, id + "F10", { "sketchPlane" : qUnion([Q0])});
            skLineSegment(sketch, "E332", {"start": v(-116.02, 43) * mm, "end": v(-116.02, 48) * mm});
            skLineSegment(sketch, "E333", {"start": v(-116.02, 55) * mm, "end": v(-116.02, 60) * mm});
            skLineSegment(sketch, "E334", {"start": v(-116.02, 60) * mm, "end": v(3.98, 60) * mm});
            skLineSegment(sketch, "E335", {"start": v(-116.02, 55) * mm, "end": v(-109.02, 55) * mm});
            skLineSegment(sketch, "E336", {"start": v(-109.02, 55) * mm, "end": v(-116.02, 48) * mm});
            skLineSegment(sketch, "E337", {"start": v(-116.02, 43) * mm, "end": v(-104.02, 55) * mm});
            skLineSegment(sketch, "E338", {"start": v(-104.02, 55) * mm, "end": v(-81.02, 55) * mm});
            skLineSegment(sketch, "E339", {"start": v(-81.02, 55) * mm, "end": v(-81.02, -5) * mm});
            skLineSegment(sketch, "E340", {"start": v(-81.02, -5) * mm, "end": v(-76.02, -5) * mm});
            skLineSegment(sketch, "E341", {"start": v(-76.02, -5) * mm, "end": v(-76.02, 55) * mm});
            skLineSegment(sketch, "E342", {"start": v(-76.02, 55) * mm, "end": v(-41.02, 55) * mm});
            skLineSegment(sketch, "E343", {"start": v(-41.02, 55) * mm, "end": v(-41.02, -5) * mm});
            skLineSegment(sketch, "E344", {"start": v(-41.02, -5) * mm, "end": v(-36.02, -5) * mm});
            skLineSegment(sketch, "E345", {"start": v(-36.02, -5) * mm, "end": v(-36.02, 55) * mm});
            skLineSegment(sketch, "E346", {"start": v(-36.02, 55) * mm, "end": v(-8.02, 55) * mm});
            skLineSegment(sketch, "E347", {"start": v(-8.02, 55) * mm, "end": v(3.98, 43) * mm});
            skLineSegment(sketch, "E348", {"start": v(3.98, 43) * mm, "end": v(3.98, 48) * mm});
            skLineSegment(sketch, "E349", {"start": v(3.98, 48) * mm, "end": v(-3.02, 55) * mm});
            skLineSegment(sketch, "E350", {"start": v(-3.02, 55) * mm, "end": v(3.98, 55) * mm});
            skLineSegment(sketch, "E351", {"start": v(3.98, 55) * mm, "end": v(3.98, 60) * mm});
            skLineSegment(sketch, "E352", {"start": v(8.98, 60) * mm, "end": v(73.98, 60) * mm});
            skLineSegment(sketch, "E353", {"start": v(8.98, 60) * mm, "end": v(8.98, 55) * mm});
            skLineSegment(sketch, "E354", {"start": v(73.98, 60) * mm, "end": v(73.98, 55) * mm});
            skLineSegment(sketch, "E355", {"start": v(8.98, 55) * mm, "end": v(15.98, 55) * mm});
            skLineSegment(sketch, "E356", {"start": v(8.98, 55) * mm, "end": v(8.98, 48) * mm});
            skLineSegment(sketch, "E357", {"start": v(8.98, 48) * mm, "end": v(8.98, 43) * mm});
            skLineSegment(sketch, "E358", {"start": v(15.98, 55) * mm, "end": v(20.98, 55) * mm});
            skLineSegment(sketch, "E359", {"start": v(8.98, 48) * mm, "end": v(15.98, 55) * mm});
            skLineSegment(sketch, "E360", {"start": v(8.98, 43) * mm, "end": v(20.98, 55) * mm});
            skLineSegment(sketch, "E361", {"start": v(73.98, 55) * mm, "end": v(66.98, 55) * mm});
            skLineSegment(sketch, "E362", {"start": v(66.98, 55) * mm, "end": v(61.98, 55) * mm});
            skLineSegment(sketch, "E363", {"start": v(73.98, 55) * mm, "end": v(73.98, 48) * mm});
            skLineSegment(sketch, "E364", {"start": v(73.98, 48) * mm, "end": v(73.98, 43) * mm});
            skLineSegment(sketch, "E365", {"start": v(66.98, 55) * mm, "end": v(73.98, 48) * mm});
            skLineSegment(sketch, "E366", {"start": v(61.98, 55) * mm, "end": v(73.98, 43) * mm});
            skLineSegment(sketch, "E367", {"start": v(20.98, 55) * mm, "end": v(38.98, 55) * mm});
            skLineSegment(sketch, "E368", {"start": v(61.98, 55) * mm, "end": v(43.98, 55) * mm});
            skLineSegment(sketch, "E369", {"start": v(38.98, 55) * mm, "end": v(38.98, -5) * mm});
            skLineSegment(sketch, "E370", {"start": v(43.98, 55) * mm, "end": v(43.98, -5) * mm});
            skLineSegment(sketch, "E371", {"start": v(38.98, -5) * mm, "end": v(43.98, -5) * mm});
            skSolve(sketch);
        }
        {
            var Q0;
            Q0 = qSketchRegion(id + "F10", true);
            extrude(context, id + "F11", {"entities" : qUnion([Q0]), "oppositeDirection" : true, "depth" : 5 * mm});
        }
    });
